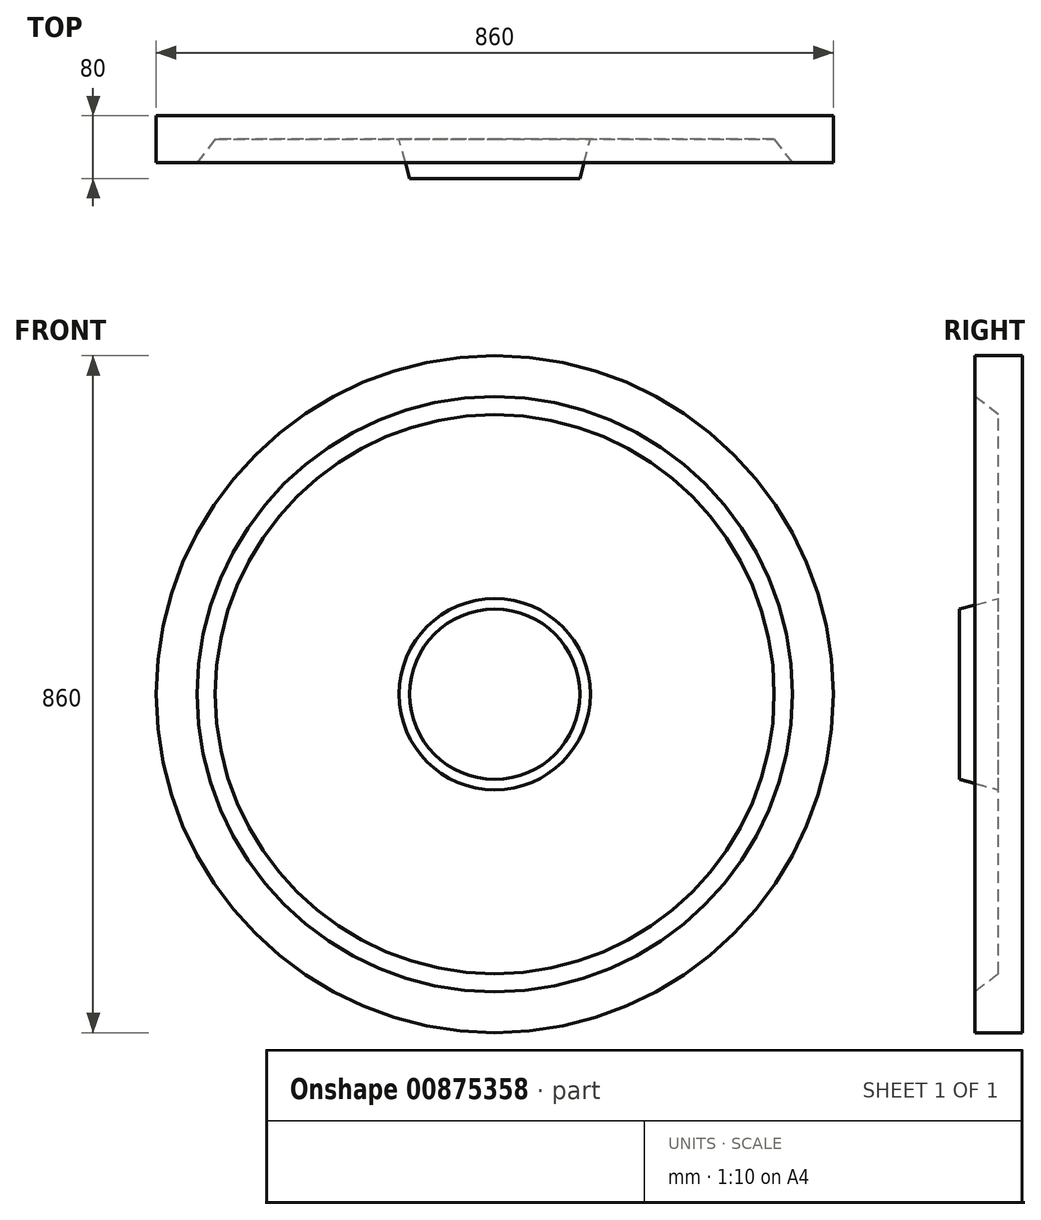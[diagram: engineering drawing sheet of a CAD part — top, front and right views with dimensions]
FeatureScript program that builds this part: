
annotation { "Feature Type Name" : "Feature", "Feature Type Description" : "" }
export const myFeature = defineFeature(function(context is Context, id is Id, definition is map)
    precondition{}
    {
        {
            var Q0;
            Q0=qCreatedBy(makeId("Front.planeOp"),FACE);
            var sketch = newSketch(context, id + "F0", { "sketchPlane" : qUnion([Q0])});
            skCircle(sketch, "E0", {"center": v(0, 0) * mm, "radius": 430 * mm});
            skSolve(sketch);
        }
        {
            var Q0;
            Q0 = qSketchRegion(id + "F0", true);
            extrude(context, id + "F1", {"entities" : qUnion([Q0]), "endBound" : BoundingType.SYMMETRIC, "depth" : 60 * mm, "offsetDistance" : 25 * mm});
        }
        {
            var Q0;
            Q0=makeQuery(id+"F1.opExtrude","CAP_FACE",FACE,{"disambiguationData":[OSD([sQuery(id+"F0.wireOp",EDGE,"E0")])],"isStart":false});
            var sketch = newSketch(context, id + "F2", { "sketchPlane" : qUnion([Q0])});
            skCircle(sketch, "E1", {"center": v(0, 0) * mm, "radius": 385 * mm});
            skCircle(sketch, "E2", {"center": v(0, 0) * mm, "radius": 100 * mm});
            skSolve(sketch);
        }
        {
            var Q0;
            Q0=makeQuery(id+"F2.imprint","IMPRINT",FACE,{"disambiguationData":[TD([[makeQuery(id+"F2.imprint","IMPRINT",EDGE,{"derivedFrom":sQuery(id+"F2.wireOp",EDGE,"E1")}),1.0]])]});
            extrude(context, id + "F3", {"entities" : qUnion([Q0]), "operationType" : NewBodyOperationType.REMOVE, "oppositeDirection" : true, "depth" : 30 * mm, "offsetDistance" : 25 * mm});
        }
        {
            var Q0;
            Q0=makeQuery(id+"F3.boolean.opBoolean","SPLIT",FACE,{"disambiguationData":[TD([makeQuery(id+"F3.opExtrude","SWEPT_FACE",FACE,{"disambiguationData":[OSD([sQuery(id+"F2.wireOp",EDGE,"E2")])]})])],"derivedFrom":makeQuery(id+"F1.opExtrude","CAP_FACE",FACE,{"disambiguationData":[OSD([sQuery(id+"F0.wireOp",EDGE,"E0")])],"isStart":false})});
            extrude(context, id + "F4", {"entities" : qUnion([Q0]), "operationType" : NewBodyOperationType.ADD, "depth" : 20 * mm, "offsetDistance" : 25 * mm});
        }
        {
            var Q0;
            Q0=makeQuery(id+"F3.boolean.opBoolean","COPY",EDGE,{"derivedFrom":makeQuery(id+"F3.opExtrude","CAP_EDGE",EDGE,{"disambiguationData":[OSD([sQuery(id+"F2.wireOp",EDGE,"E2")])],"isStart":false})});
            chamfer(context, id + "F5", {"entities" : qUnion([Q0]), "chamferType" : ChamferType.OFFSET_ANGLE, "width" : 80 * mm, "oppositeDirection" : false, "angle" : 15 * degree, "tangentPropagation" : true});
        }
        {
            var Q0;
            Q0=makeQuery(id+"F3.boolean.opBoolean","COPY",EDGE,{"derivedFrom":makeQuery(id+"F3.opExtrude","CAP_EDGE",EDGE,{"disambiguationData":[OSD([sQuery(id+"F2.wireOp",EDGE,"E1")])],"isStart":false})});
            chamfer(context, id + "F6", {"entities" : qUnion([Q0]), "chamferType" : ChamferType.OFFSET_ANGLE, "width" : 30 * mm, "oppositeDirection" : false, "angle" : 52.5 * degree, "tangentPropagation" : true});
        }
    });
